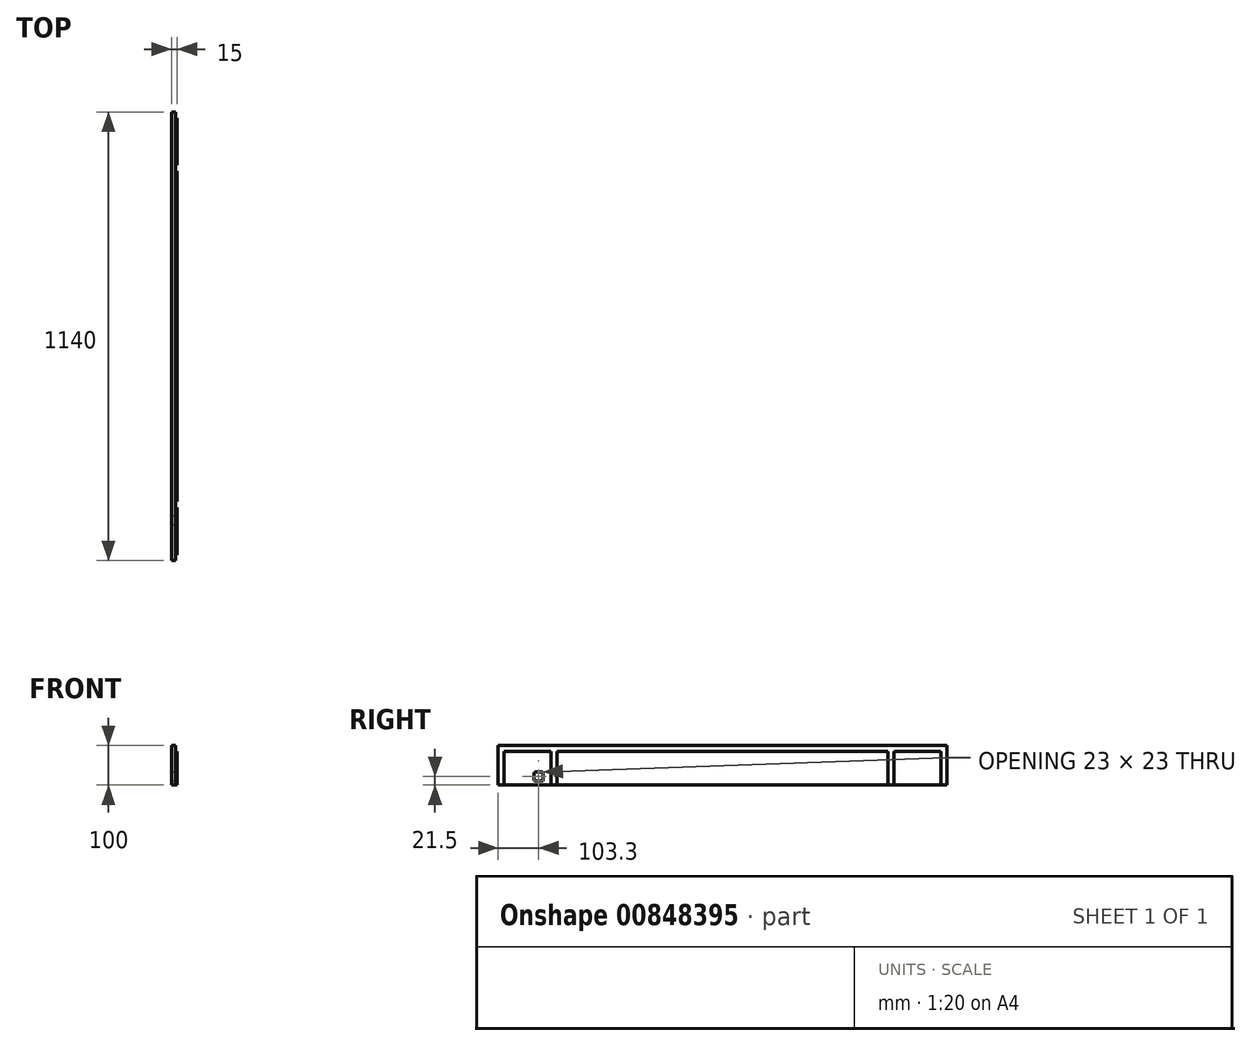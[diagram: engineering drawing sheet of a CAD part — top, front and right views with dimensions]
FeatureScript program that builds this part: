
annotation { "Feature Type Name" : "Feature", "Feature Type Description" : "" }
export const myFeature = defineFeature(function(context is Context, id is Id, definition is map)
    precondition{}
    {
        {
            var Q0;
            Q0=qCreatedBy(makeId("Top.planeOp"),FACE);
            var sketch = newSketch(context, id + "F0", { "sketchPlane" : qUnion([Q0])});
            skLineSegment(sketch, "E0", {"start": v(0, 0) * mm, "end": v(0, -555) * mm});
            skLineSegment(sketch, "E1", {"start": v(0, -555) * mm, "end": v(-5, -555) * mm});
            skLineSegment(sketch, "E2", {"start": v(-5, -555) * mm, "end": v(-5, -570) * mm});
            skLineSegment(sketch, "E3", {"start": v(-5, -570) * mm, "end": v(-15, -570) * mm});
            skLineSegment(sketch, "E4", {"start": v(-15, -570) * mm, "end": v(-15, 0) * mm});
            skLineSegment(sketch, "E5", {"start": v(-15, 0) * mm, "end": v(0, 0) * mm});
            skSolve(sketch);
        }
        {
            var Q0;
            Q0=qSketchRegion(id+"F0",true);
            extrude(context, id + "F1", {"entities" : qUnion([Q0]), "endBound" : BoundingType.SYMMETRIC, "depth" : 100 * mm, "offsetDistance" : 25 * mm});
        }
        {
            var Q0;
            Q0=makeQuery(id+"F1.opExtrude","SWEPT_FACE",FACE,{"disambiguationData":[OSD([sQuery(id+"F0.wireOp",EDGE,"E0")])]});
            var sketch = newSketch(context, id + "F2", { "sketchPlane" : qUnion([Q0])});
            skLineSegment(sketch, "E6", {"start": v(-435.2, -50) * mm, "end": v(-435.2, 34.8) * mm});
            skLineSegment(sketch, "E7", {"start": v(-420, 34.8) * mm, "end": v(-420, -50) * mm});
            skLineSegment(sketch, "E8", {"start": v(-420, -50) * mm, "end": v(-435.2, -50) * mm});
            skLineSegment(sketch, "E9", {"start": v(-420, 34.8) * mm, "end": v(0, 34.8) * mm});
            skLineSegment(sketch, "E10", {"start": v(0, 34.8) * mm, "end": v(0, 50) * mm});
            skLineSegment(sketch, "E11", {"start": v(0, 50) * mm, "end": v(-555, 50) * mm});
            skLineSegment(sketch, "E12", {"start": v(-555, 50) * mm, "end": v(-555, 34.8) * mm});
            skLineSegment(sketch, "E13", {"start": v(-555, 34.8) * mm, "end": v(-435.2, 34.8) * mm});
            skSolve(sketch);
        }
        {
            var Q0;
            Q0=qSketchRegion(id+"F2",true);
            extrude(context, id + "F3", {"entities" : qUnion([Q0]), "operationType" : NewBodyOperationType.REMOVE, "oppositeDirection" : true, "depth" : 5 * mm, "offsetDistance" : 25 * mm});
        }
        {
            var Q0;
            Q0=makeQuery(id+"F1.opExtrude","SWEPT_BODY",BODY,{"disambiguationData":[OSD([sQuery(id+"F0.wireOp",EDGE,"E0"),sQuery(id+"F0.wireOp",EDGE,"E1"),sQuery(id+"F0.wireOp",EDGE,"E2"),sQuery(id+"F0.wireOp",EDGE,"E3"),sQuery(id+"F0.wireOp",EDGE,"E4"),sQuery(id+"F0.wireOp",EDGE,"E5")])]});
            var Q1;
            Q1=makeQuery(id+"F1.opExtrude","SWEPT_FACE",FACE,{"disambiguationData":[OSD([sQuery(id+"F0.wireOp",EDGE,"E5")])]});
            mirror(context, id + "F4", {"operationType" : NewBodyOperationType.ADD, "entities" : qUnion([Q0]), "mirrorPlane" : qUnion([Q1])});
        }
        {
            var Q0;
            {var subQ0=sQuery(id+"F0.wireOp",EDGE,"E1");var subQ1=sQuery(id+"F0.wireOp",EDGE,"E0");Q0=makeQuery(id+"F3.boolean.opBoolean","SPLIT",FACE,{"disambiguationData":[TD([makeQuery(id+"F1.opExtrude","SWEPT_FACE",FACE,{"disambiguationData":[OSD([subQ0])]})])],"derivedFrom":makeQuery(id+"F1.opExtrude","SWEPT_FACE",FACE,{"disambiguationData":[OSD([subQ1])]})});}
            var sketch = newSketch(context, id + "F5", { "sketchPlane" : qUnion([Q0])});
            skLineSegment(sketch, "E14", {"start": v(-478.2, -37) * mm, "end": v(-478.2, -20) * mm});
            skArc(sketch, "E15", {"start": v(-478.2, -20) * mm, "mid": v(-477.32, -17.88) * mm, "end": v(-475.2, -17) * mm});
            skLineSegment(sketch, "E16", {"start": v(-475.2, -17) * mm, "end": v(-458.2, -17) * mm});
            skArc(sketch, "E17", {"start": v(-458.2, -17) * mm, "mid": v(-456.08, -17.88) * mm, "end": v(-455.2, -20) * mm});
            skLineSegment(sketch, "E18", {"start": v(-455.2, -20) * mm, "end": v(-455.2, -37) * mm});
            skArc(sketch, "E19", {"start": v(-478.2, -37) * mm, "mid": v(-477.32, -39.12) * mm, "end": v(-475.2, -40) * mm});
            skLineSegment(sketch, "E20", {"start": v(-475.2, -40) * mm, "end": v(-458.2, -40) * mm});
            skArc(sketch, "E21", {"start": v(-458.2, -40) * mm, "mid": v(-456.08, -39.12) * mm, "end": v(-455.2, -37) * mm});
            skSolve(sketch);
        }
        {
            var Q0;
            Q0 = qSketchRegion(id + "F5", true);
            extrude(context, id + "F6", {"entities" : qUnion([Q0]), "operationType" : NewBodyOperationType.REMOVE, "endBound" : BoundingType.UP_TO_NEXT, "oppositeDirection" : true, "depth" : 25 * mm, "offsetDistance" : 25 * mm});
        }
        {
            var Q0;
            Q0=qCreatedBy(makeId("Right.planeOp"),FACE);
            cPlane(context, id + "F7", {"entities" : qUnion([Q0]), "cplaneType" : CPlaneType.OFFSET, "offset" : 25 * mm, "width" : 150 * mm, "height" : 150 * mm});
        }
    });
